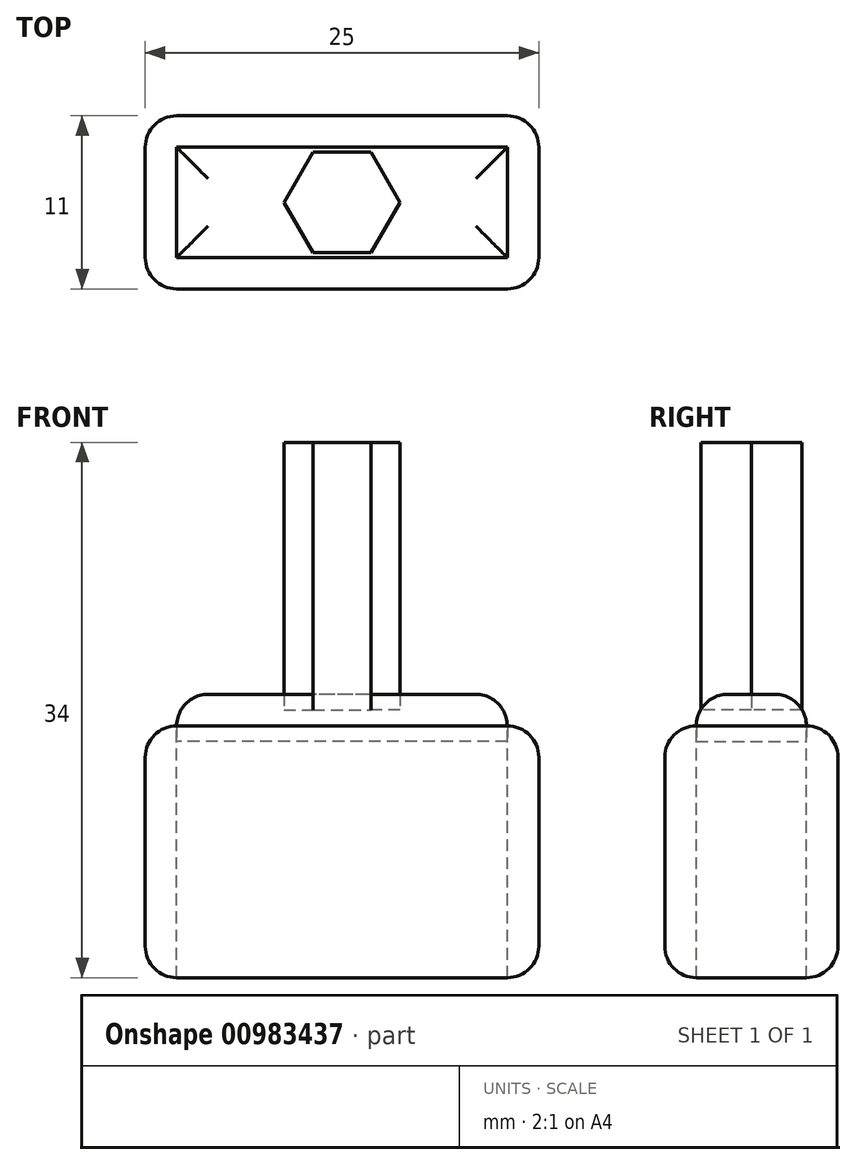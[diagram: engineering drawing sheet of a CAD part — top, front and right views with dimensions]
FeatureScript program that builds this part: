
annotation { "Feature Type Name" : "Feature", "Feature Type Description" : "" }
export const myFeature = defineFeature(function(context is Context, id is Id, definition is map)
    precondition{}
    {
        {
            var Q0;
            Q0=qCreatedBy(makeId("Top.planeOp"),FACE);
            var sketch = newSketch(context, id + "F0", { "sketchPlane" : qUnion([Q0])});
            skCircle(sketch, "E0.cCircle", {"center": v(0, 0) * mm, "radius": 3.2 * mm, "construction": true});
            skLineSegment(sketch, "E0.0", {"start": v(3.7, 0) * mm, "end": v(1.85, -3.2) * mm});
            skLineSegment(sketch, "E0.1", {"start": v(1.85, -3.2) * mm, "end": v(-1.85, -3.2) * mm});
            skLineSegment(sketch, "E0.2", {"start": v(-1.85, -3.2) * mm, "end": v(-3.7, 0) * mm});
            skLineSegment(sketch, "E0.3", {"start": v(-3.7, 0) * mm, "end": v(-1.85, 3.2) * mm});
            skLineSegment(sketch, "E0.4", {"start": v(-1.85, 3.2) * mm, "end": v(1.85, 3.2) * mm});
            skLineSegment(sketch, "E0.5", {"start": v(1.85, 3.2) * mm, "end": v(3.7, 0) * mm});
            skPoint(sketch, "E0.0.midPoint", {"position": v(2.77, -1.6) * mm});
            skSolve(sketch);
        }
        {
            var Q0;
            Q0 = qSketchRegion(id + "F0", true);
            extrude(context, id + "F1", {"entities" : qUnion([Q0]), "depth" : 17 * mm, "offsetDistance" : 25 * mm});
        }
        {
            var Q0;
            Q0=qCreatedBy(makeId("Top.planeOp"),FACE);
            var sketch = newSketch(context, id + "F2", { "sketchPlane" : qUnion([Q0])});
            skLineSegment(sketch, "E1.bottom", {"start": v(10.5, -3.5) * mm, "end": v(-10.5, -3.5) * mm});
            skLineSegment(sketch, "E1.top", {"start": v(10.5, 3.5) * mm, "end": v(-10.5, 3.5) * mm});
            skLineSegment(sketch, "E1.left", {"start": v(10.5, -3.5) * mm, "end": v(10.5, 3.5) * mm});
            skLineSegment(sketch, "E1.right", {"start": v(-10.5, -3.5) * mm, "end": v(-10.5, 3.5) * mm});
            skPoint(sketch, "E1.middle", {"position": v(0, 0) * mm});
            skLineSegment(sketch, "E2.bottom", {"start": v(12.5, -5.5) * mm, "end": v(-12.5, -5.5) * mm});
            skLineSegment(sketch, "E2.top", {"start": v(12.5, 5.5) * mm, "end": v(-12.5, 5.5) * mm});
            skLineSegment(sketch, "E2.left", {"start": v(12.5, -5.5) * mm, "end": v(12.5, 5.5) * mm});
            skLineSegment(sketch, "E2.right", {"start": v(-12.5, -5.5) * mm, "end": v(-12.5, 5.5) * mm});
            skSolve(sketch);
        }
        {
            var Q0;
            Q0=makeQuery(id+"F2.imprint","IMPRINT",FACE,{"disambiguationData":[TD([[makeQuery(id+"F2.imprint","IMPRINT",EDGE,{"derivedFrom":sQuery(id+"F2.wireOp",EDGE,"E1.bottom")}),1.0]])]});
            var Q1;
            Q1=sQuery(id+"F2.wireOp",EDGE,"E2.bottom");
            var Q2;
            Q2=sQuery(id+"F2.wireOp",EDGE,"E1.bottom");
            var Q3;
            Q3=sQuery(id+"F2.wireOp",EDGE,"E1.left");
            var Q4;
            Q4=sQuery(id+"F2.wireOp",EDGE,"E2.left");
            var Q5;
            Q5=sQuery(id+"F2.wireOp",EDGE,"E2.top");
            var Q6;
            Q6=sQuery(id+"F2.wireOp",EDGE,"E1.top");
            var Q7;
            Q7=sQuery(id+"F2.wireOp",EDGE,"E1.right");
            var Q8;
            Q8=sQuery(id+"F2.wireOp",EDGE,"E2.right");
            extrude(context, id + "F3", {"entities" : qUnion([Q0]), "surfaceEntities" : qUnion([Q1, Q2, Q3, Q4, Q5, Q6, Q7, Q8]), "depth" : -17 * mm, "offsetDistance" : 25 * mm, "hasSecondDirection" : true, "secondDirectionOppositeDirection" : true, "secondDirectionDepth" : 1 * mm});
        }
        {
            var Q0;
            Q0=makeQuery(id+"F2.imprint","IMPRINT",FACE,{"disambiguationData":[TD([[makeQuery(id+"F2.imprint","IMPRINT",EDGE,{"derivedFrom":sQuery(id+"F2.wireOp",EDGE,"E1.bottom")}),-1.0]])]});
            extrude(context, id + "F4", {"entities" : qUnion([Q0]), "depth" : 1 * mm, "offsetDistance" : 25 * mm, "hasSecondDirection" : true, "secondDirectionOppositeDirection" : true, "secondDirectionDepth" : 2 * mm});
        }
        {
            var Q0;
            Q0=makeQuery(id+"F4.opExtrude","CAP_FACE",FACE,{"disambiguationData":[OSD([sQuery(id+"F2.wireOp",EDGE,"E1.bottom"),sQuery(id+"F2.wireOp",EDGE,"E1.top"),sQuery(id+"F2.wireOp",EDGE,"E1.left"),sQuery(id+"F2.wireOp",EDGE,"E1.right")])],"isStart":false});
            fillet(context, id + "F5", {"entities" : qUnion([Q0]), "radius" : 2 * mm, "tangentPropagation" : true, "allowEdgeOverflow" : false});
        }
        {
            var Q0;
            Q0=makeQuery(id+"F3.opExtrude","SWEPT_FACE",FACE,{"disambiguationData":[OSD([sQuery(id+"F2.wireOp",EDGE,"E2.top")])]});
            var Q1;
            Q1=makeQuery(id+"F3.opExtrude","SWEPT_FACE",FACE,{"disambiguationData":[OSD([sQuery(id+"F2.wireOp",EDGE,"E2.bottom")])]});
            var Q2;
            Q2=makeQuery(id+"F3.opExtrude","SWEPT_FACE",FACE,{"disambiguationData":[OSD([sQuery(id+"F2.wireOp",EDGE,"E2.right")])]});
            var Q3;
            Q3=makeQuery(id+"F3.opExtrude","SWEPT_FACE",FACE,{"disambiguationData":[OSD([sQuery(id+"F2.wireOp",EDGE,"E2.left")])]});
            fillet(context, id + "F6", {"entities" : qUnion([Q0, Q1, Q2, Q3]), "radius" : 2 * mm, "tangentPropagation" : true, "allowEdgeOverflow" : false});
        }
    });
